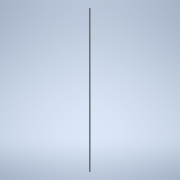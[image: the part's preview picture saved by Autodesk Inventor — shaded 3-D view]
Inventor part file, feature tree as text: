
AUTODESK INVENTOR PART (.ipt)
format: ipt  version: 2022 (Build 260153000, 153)  size: 149,504 bytes
history: native  units: mm
features: extrude x1, sketch x1
ambient origin geometry x8: Origin, YZ Plane, XZ Plane, XY Plane, X Axis, Y Axis, Z Axis, Center Point
bodies: Body1 (feature_tree)
feature tree (2):
  extrude  "Extrusion7"  Depth=5.0mm
  sketch  "Sketch4"  dims[d31=34.456mm d103=5.0mm d104=5.0mm d105=1970.0mm d106=0.0mm]
